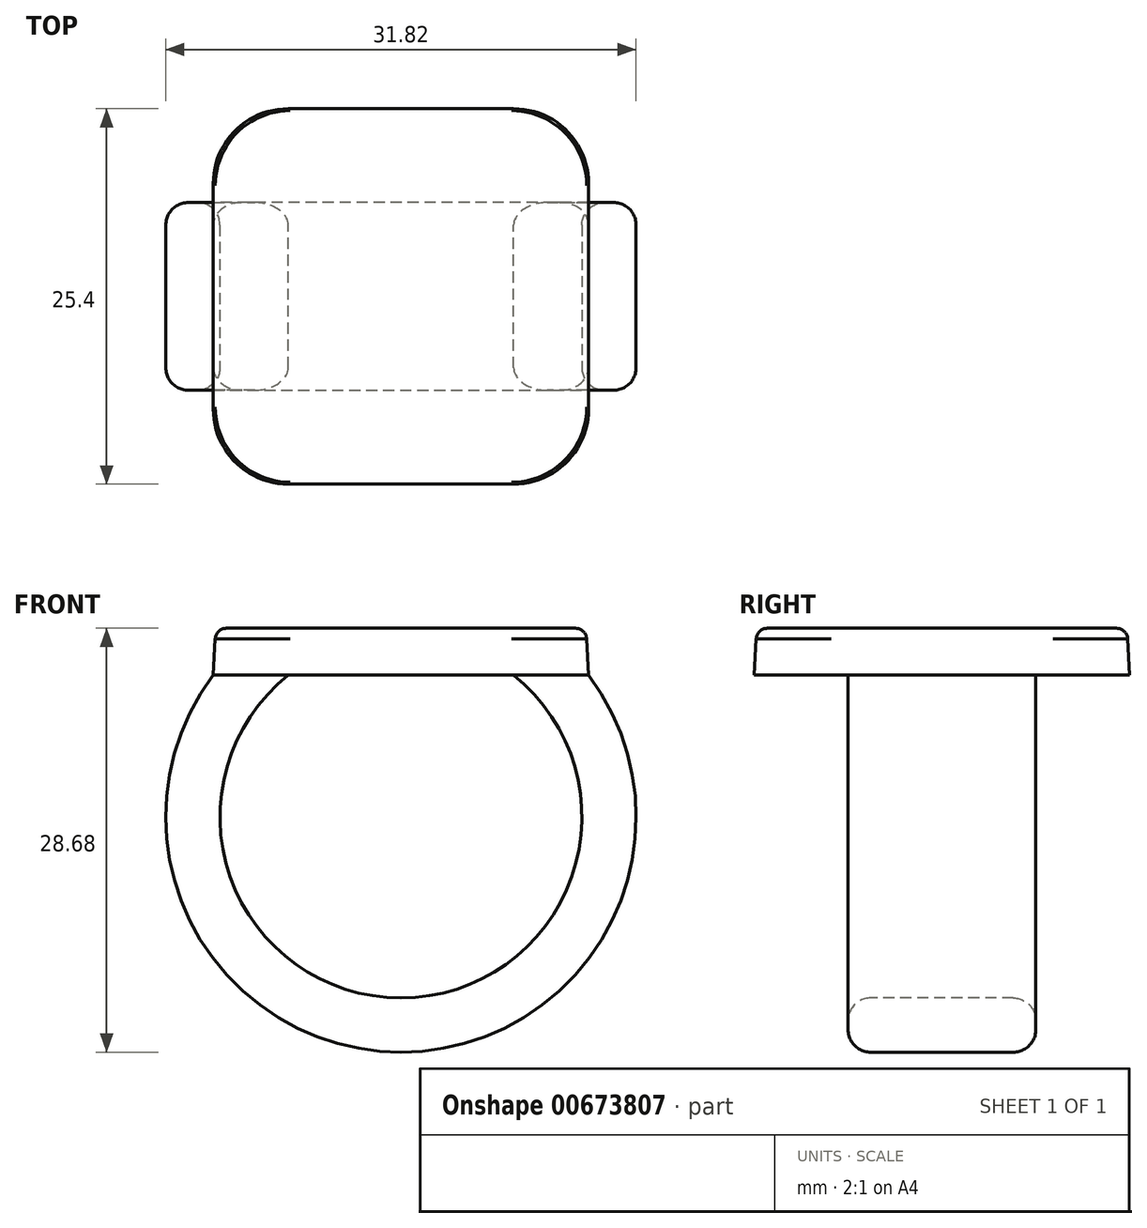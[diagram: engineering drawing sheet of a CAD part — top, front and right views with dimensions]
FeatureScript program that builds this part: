
annotation { "Feature Type Name" : "Feature", "Feature Type Description" : "" }
export const myFeature = defineFeature(function(context is Context, id is Id, definition is map)
    precondition{}
    {
        {
            var Q0;
            Q0=qCreatedBy(makeId("Top.planeOp"),FACE);
            var sketch = newSketch(context, id + "F0", { "sketchPlane" : qUnion([Q0])});
            skLineSegment(sketch, "E0.bottom", {"start": v(12.7, 12.7) * mm, "end": v(-12.7, 12.7) * mm});
            skLineSegment(sketch, "E0.top", {"start": v(12.7, -12.7) * mm, "end": v(-12.7, -12.7) * mm});
            skLineSegment(sketch, "E0.left", {"start": v(12.7, 12.7) * mm, "end": v(12.7, -12.7) * mm});
            skLineSegment(sketch, "E0.right", {"start": v(-12.7, 12.7) * mm, "end": v(-12.7, -12.7) * mm});
            skPoint(sketch, "E0.middle", {"position": v(0, 0) * mm});
            skSolve(sketch);
        }
        {
            var Q0;
            Q0 = qSketchRegion(id + "F0", true);
            extrude(context, id + "F1", {"entities" : qUnion([Q0]), "depth" : 3.17 * mm, "offsetDistance" : 25.4 * mm, "hasDraft" : true, "draftAngle" : 3 * degree, "draftPullDirection" : true});
        }
        {
            var Q0;
            Q0=qCreatedBy(makeId("Front.planeOp"),FACE);
            var sketch = newSketch(context, id + "F2", { "sketchPlane" : qUnion([Q0])});
            skArc(sketch, "E1", {"start": v(-10.16, 0) * mm, "mid": v(0, -23.56) * mm, "end": v(10.16, 0) * mm});
            skSolve(sketch);
        }
        {
            var Q0;
            Q0=makeQuery(id+"F1.opExtrude","CAP_FACE",FACE,{"disambiguationData":[OSD([sQuery(id+"F0.wireOp",EDGE,"E0.bottom"),sQuery(id+"F0.wireOp",EDGE,"E0.top"),sQuery(id+"F0.wireOp",EDGE,"E0.left"),sQuery(id+"F0.wireOp",EDGE,"E0.right")])],"isStart":true});
            var sketch = newSketch(context, id + "F3", { "sketchPlane" : qUnion([Q0])});
            skLineSegment(sketch, "E2.bottom", {"start": v(-7.62, 6.35) * mm, "end": v(-12.7, 6.35) * mm});
            skLineSegment(sketch, "E2.top", {"start": v(-7.62, -6.35) * mm, "end": v(-12.7, -6.35) * mm});
            skLineSegment(sketch, "E2.left", {"start": v(-7.62, 6.35) * mm, "end": v(-7.62, -6.35) * mm});
            skLineSegment(sketch, "E2.right", {"start": v(-12.7, 6.35) * mm, "end": v(-12.7, -6.35) * mm});
            skPoint(sketch, "E2.middle", {"position": v(-10.16, 0) * mm});
            skSolve(sketch);
        }
        {
            var Q0;
            Q0 = qSketchRegion(id + "F3", true);
            var Q1;
            Q1 = qConstructionFilter(qBodyType(qCreatedBy(id + "F2" ,EDGE), BodyType.WIRE), ConstructionObject.NO);
            sweep(context, id + "F4", {"operationType" : NewBodyOperationType.ADD, "profiles" : qUnion([Q0]), "path" : qUnion([Q1])});
        }
        {
            var Q0;
            Q0=qCreatedBy(makeId("Front.planeOp"),FACE);
            var sketch = newSketch(context, id + "F5", { "sketchPlane" : qUnion([Q0])});
            skLineSegment(sketch, "E3.0", {"start": v(10.16, 0) * mm, "end": v(7.62, 0) * mm});
            skLineSegment(sketch, "E3.1", {"start": v(10.01, -2.54) * mm, "end": v(10.16, 0) * mm});
            skArc(sketch, "E3.2", {"start": v(10.01, -2.54) * mm, "mid": v(8.9, -1.18) * mm, "end": v(7.62, 0) * mm});
            skLineSegment(sketch, "E4.trimOffspring", {"start": v(-7.62, 0) * mm, "end": v(-12.7, 0) * mm});
            skPoint(sketch, "E5.orphan", {"position": v(12.7, 0) * mm});
            skSolve(sketch);
        }
        {
            var Q0;
            Q0 = qSketchRegion(id + "F5", true);
            var Q1;
            Q1=makeQuery(id+"F4.opSweep","SWEPT_FACE",FACE,{"disambiguationData":[OSD([sQuery(id+"F2.wireOp",EDGE,"E1"),sQuery(id+"F3.wireOp",EDGE,"E2.bottom")])]});
            var Q2;
            Q2=makeQuery(id+"F4.opSweep","SWEPT_FACE",FACE,{"disambiguationData":[OSD([sQuery(id+"F2.wireOp",EDGE,"E1"),sQuery(id+"F3.wireOp",EDGE,"E2.top")])]});
            extrude(context, id + "F6", {"entities" : qUnion([Q0]), "operationType" : NewBodyOperationType.ADD, "endBound" : BoundingType.UP_TO_SURFACE, "depth" : 25.4 * mm, "endBoundEntityFace" : qUnion([Q1]), "offsetDistance" : 25.4 * mm, "hasSecondDirection" : true, "secondDirectionBound" : BoundingType.UP_TO_SURFACE, "secondDirectionOppositeDirection" : true, "secondDirectionDepth" : 25.4 * mm, "secondDirectionBoundEntityFace" : qUnion([Q2])});
        }
        {
            var Q0;
            Q0=makeQuery(id+"F1.opExtrude","SWEPT_EDGE",EDGE,{"disambiguationData":[OSD([sQuery(id+"F0.wireOp",EDGE,"E0.top"),sQuery(id+"F0.wireOp",EDGE,"E0.right")])]});
            var Q1;
            Q1=makeQuery(id+"F1.opExtrude","SWEPT_EDGE",EDGE,{"disambiguationData":[OSD([sQuery(id+"F0.wireOp",EDGE,"E0.bottom"),sQuery(id+"F0.wireOp",EDGE,"E0.right")])]});
            var Q2;
            Q2=makeQuery(id+"F1.opExtrude","SWEPT_EDGE",EDGE,{"disambiguationData":[OSD([sQuery(id+"F0.wireOp",EDGE,"E0.top"),sQuery(id+"F0.wireOp",EDGE,"E0.left")])]});
            var Q3;
            Q3=makeQuery(id+"F1.opExtrude","SWEPT_EDGE",EDGE,{"disambiguationData":[OSD([sQuery(id+"F0.wireOp",EDGE,"E0.bottom"),sQuery(id+"F0.wireOp",EDGE,"E0.left")])]});
            fillet(context, id + "F7", {"entities" : qUnion([Q0, Q1, Q2, Q3]), "radius" : 5.08 * mm, "tangentPropagation" : true, "allowEdgeOverflow" : false});
        }
        {
            var Q0;
            {var subQ0=sQuery(id+"F3.wireOp",EDGE,"E2.bottom");var subQ1=sQuery(id+"F2.wireOp",EDGE,"E1");Q0=makeQuery(id+"F6.boolean.opBoolean","MERGE",EDGE,{"derivedFrom":[makeQuery(id+"F4.opSweep","SWEPT_EDGE",EDGE,{"disambiguationData":[OSD([subQ1,subQ0,sQuery(id+"F3.wireOp",EDGE,"E2.left")])]}),makeQuery(id+"F6.opExtrude","TWEAK_EDGE",EDGE,{"derivedFrom":[makeQuery(id+"F4.opSweep","SWEPT_FACE",FACE,{"disambiguationData":[OSD([subQ1,subQ0])]}),makeQuery(id+"F5.imprint","IMPRINT",EDGE,{"derivedFrom":sQuery(id+"F5.wireOp",EDGE,"E3.2")})]})]});}
            var Q1;
            Q1=makeQuery(id+"F4.opSweep","SWEPT_EDGE",EDGE,{"disambiguationData":[OSD([sQuery(id+"F0.wireOp",EDGE,"E0.right"),sQuery(id+"F2.wireOp",EDGE,"E1"),sQuery(id+"F3.wireOp",EDGE,"E2.bottom"),sQuery(id+"F3.wireOp",EDGE,"E2.right")])]});
            var Q2;
            {var subQ0=sQuery(id+"F3.wireOp",EDGE,"E2.top");var subQ1=sQuery(id+"F2.wireOp",EDGE,"E1");Q2=makeQuery(id+"F6.boolean.opBoolean","MERGE",EDGE,{"derivedFrom":[makeQuery(id+"F4.opSweep","SWEPT_EDGE",EDGE,{"disambiguationData":[OSD([subQ1,subQ0,sQuery(id+"F3.wireOp",EDGE,"E2.left")])]}),makeQuery(id+"F6.opExtrude","TWEAK_EDGE",EDGE,{"derivedFrom":[makeQuery(id+"F4.opSweep","SWEPT_FACE",FACE,{"disambiguationData":[OSD([subQ1,subQ0])]}),makeQuery(id+"F5.imprint","IMPRINT",EDGE,{"derivedFrom":sQuery(id+"F5.wireOp",EDGE,"E3.2")})]})]});}
            var Q3;
            Q3=makeQuery(id+"F4.opSweep","SWEPT_EDGE",EDGE,{"disambiguationData":[OSD([sQuery(id+"F0.wireOp",EDGE,"E0.right"),sQuery(id+"F2.wireOp",EDGE,"E1"),sQuery(id+"F3.wireOp",EDGE,"E2.top"),sQuery(id+"F3.wireOp",EDGE,"E2.right")])]});
            fillet(context, id + "F8", {"entities" : qUnion([Q0, Q1, Q2, Q3]), "radius" : 1.52 * mm, "tangentPropagation" : true, "allowEdgeOverflow" : false});
        }
        {
            var Q0;
            Q0=makeQuery(id+"F1.opExtrude","CAP_FACE",FACE,{"disambiguationData":[OSD([sQuery(id+"F0.wireOp",EDGE,"E0.bottom"),sQuery(id+"F0.wireOp",EDGE,"E0.top"),sQuery(id+"F0.wireOp",EDGE,"E0.left"),sQuery(id+"F0.wireOp",EDGE,"E0.right")])],"isStart":false});
            fillet(context, id + "F9", {"entities" : qUnion([Q0]), "radius" : 0.76 * mm, "tangentPropagation" : true, "allowEdgeOverflow" : false});
        }
    });
